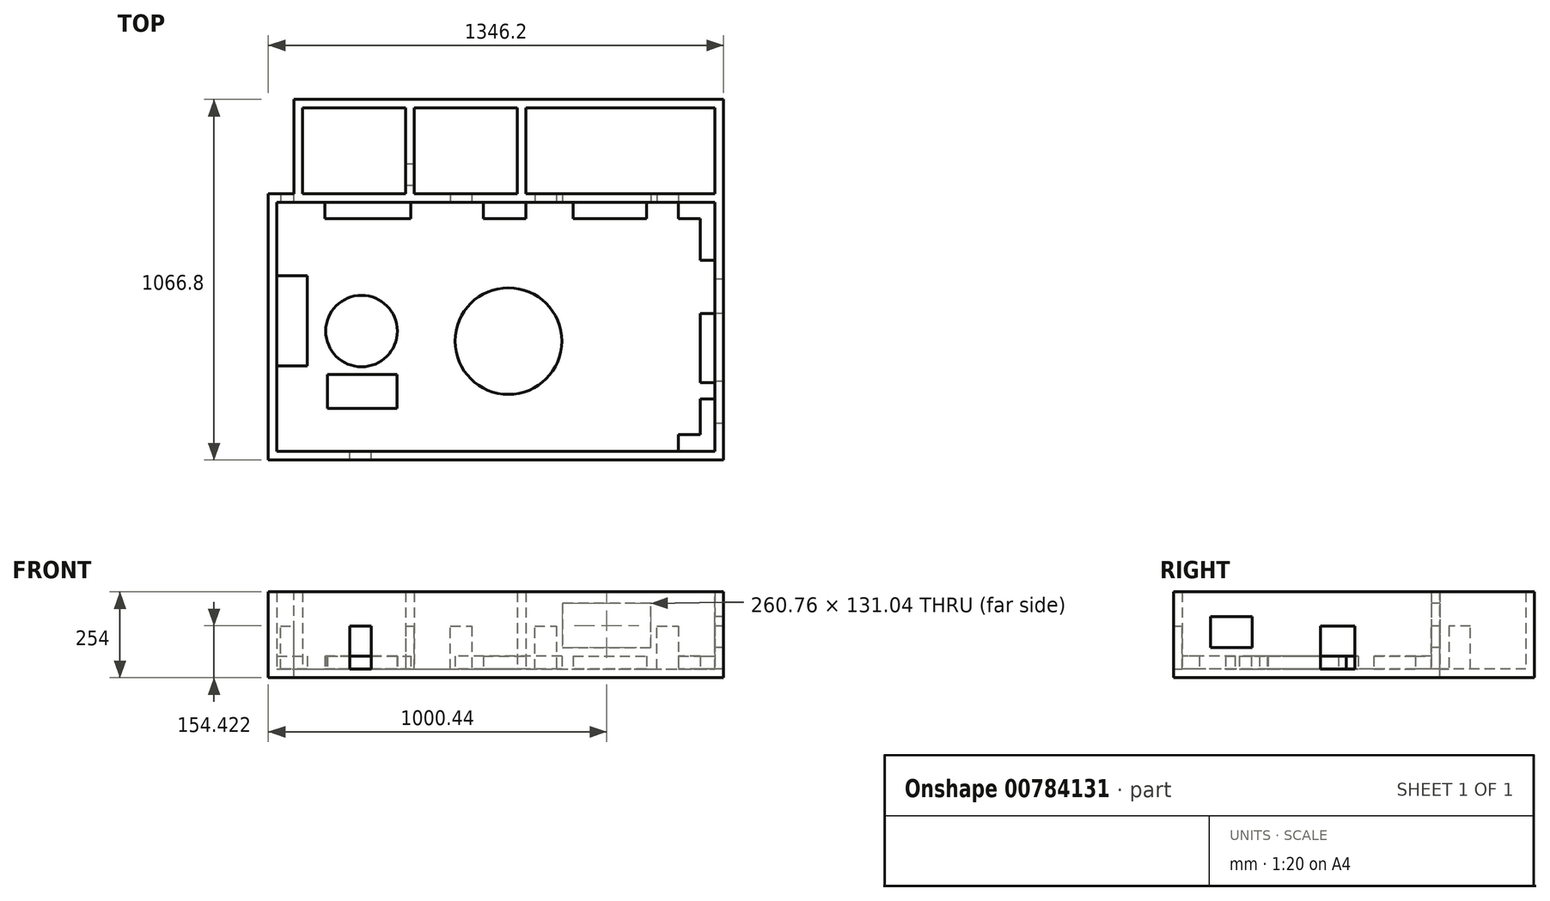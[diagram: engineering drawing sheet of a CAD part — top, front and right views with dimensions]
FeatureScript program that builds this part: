
annotation { "Feature Type Name" : "Feature", "Feature Type Description" : "" }
export const myFeature = defineFeature(function(context is Context, id is Id, definition is map)
    precondition{}
    {
        {
            var Q0;
            Q0=qCreatedBy(makeId("Top.planeOp"),FACE);
            var sketch = newSketch(context, id + "F0", { "sketchPlane" : qUnion([Q0])});
            skLineSegment(sketch, "E0.bottom", {"start": v(-673.24, 405.83) * mm, "end": v(672.96, 405.83) * mm});
            skLineSegment(sketch, "E0.top", {"start": v(-673.24, -381.57) * mm, "end": v(672.96, -381.57) * mm});
            skLineSegment(sketch, "E0.left", {"start": v(-673.24, 405.83) * mm, "end": v(-673.24, -381.57) * mm});
            skLineSegment(sketch, "E0.right", {"start": v(672.96, 405.83) * mm, "end": v(672.96, -381.57) * mm});
            skSolve(sketch);
        }
        {
            var Q0;
            Q0 = qSketchRegion(id + "F0", true);
            extrude(context, id + "F1", {"entities" : qUnion([Q0]), "depth" : 254 * mm, "offsetDistance" : 25.4 * mm});
        }
        {
            var Q0;
            Q0=makeQuery(id+"F1.opExtrude","CAP_FACE",FACE,{"disambiguationData":[OSD([sQuery(id+"F0.wireOp",EDGE,"E0.bottom"),sQuery(id+"F0.wireOp",EDGE,"E0.top"),sQuery(id+"F0.wireOp",EDGE,"E0.left"),sQuery(id+"F0.wireOp",EDGE,"E0.right")])],"isStart":false});
            shell(context, id + "F2", {"entities" : qUnion([Q0]), "thickness" : 25.4 * mm});
        }
        {
            var Q0;
            Q0=makeQuery(id+"F1.opExtrude","SWEPT_FACE",FACE,{"disambiguationData":[OSD([sQuery(id+"F0.wireOp",EDGE,"E0.bottom")])]});
            var sketch = newSketch(context, id + "F3", { "sketchPlane" : qUnion([Q0])});
            skLineSegment(sketch, "E1", {"start": v(597.04, 0) * mm, "end": v(597.04, 254) * mm});
            skLineSegment(sketch, "E2", {"start": v(597.04, 254) * mm, "end": v(-672.96, 254) * mm});
            skLineSegment(sketch, "E3", {"start": v(-672.96, 254) * mm, "end": v(-672.96, 0) * mm});
            skLineSegment(sketch, "E4", {"start": v(-672.96, 0) * mm, "end": v(597.04, 0) * mm});
            skSolve(sketch);
        }
        {
            var Q0;
            Q0 = qSketchRegion(id + "F3", true);
            extrude(context, id + "F4", {"entities" : qUnion([Q0]), "operationType" : NewBodyOperationType.ADD, "depth" : 279.4 * mm, "offsetDistance" : 25.4 * mm});
        }
        {
            var Q0;
            Q0=makeQuery(id+"F4.boolean.opBoolean","MERGE",FACE,{"derivedFrom":[makeQuery(id+"F1.opExtrude","CAP_FACE",FACE,{"disambiguationData":[OSD([sQuery(id+"F0.wireOp",EDGE,"E0.bottom"),sQuery(id+"F0.wireOp",EDGE,"E0.top"),sQuery(id+"F0.wireOp",EDGE,"E0.left"),sQuery(id+"F0.wireOp",EDGE,"E0.right")])],"isStart":false}),makeQuery(id+"F4.opExtrude","SWEPT_FACE",FACE,{"disambiguationData":[OSD([sQuery(id+"F3.wireOp",EDGE,"E2")])]})]});
            shell(context, id + "F5", {"entities" : qUnion([Q0]), "thickness" : 25.4 * mm});
        }
        {
            var Q0;
            Q0=makeQuery(id+"F5.opShell","OFFSET_FACE",FACE,{"disambiguationData":[OSD([sQuery(id+"F0.wireOp",EDGE,"E0.bottom"),sQuery(id+"F0.wireOp",EDGE,"E0.top"),sQuery(id+"F0.wireOp",EDGE,"E0.left"),sQuery(id+"F0.wireOp",EDGE,"E0.right"),sQuery(id+"F3.wireOp",EDGE,"E4")])]});
            var sketch = newSketch(context, id + "F6", { "sketchPlane" : qUnion([Q0])});
            skLineSegment(sketch, "E5", {"start": v(-266.84, 405.83) * mm, "end": v(-266.84, 659.83) * mm});
            skLineSegment(sketch, "E6", {"start": v(-266.84, 659.83) * mm, "end": v(-241.44, 659.83) * mm});
            skLineSegment(sketch, "E7", {"start": v(-241.44, 659.83) * mm, "end": v(-241.44, 405.83) * mm});
            skLineSegment(sketch, "E8", {"start": v(-241.44, 405.83) * mm, "end": v(-266.84, 405.83) * mm});
            skSolve(sketch);
        }
        {
            var Q0;
            Q0=makeQuery(id+"F6.imprint","IMPRINT",FACE,{"disambiguationData":[TD([[makeQuery(id+"F6.imprint","IMPRINT",EDGE,{"derivedFrom":sQuery(id+"F6.wireOp",EDGE,"E5")}),-1.0]])]});
            extrude(context, id + "F7", {"entities" : qUnion([Q0]), "operationType" : NewBodyOperationType.ADD, "depth" : 228.6 * mm, "offsetDistance" : 25.4 * mm});
        }
        {
            var Q0;
            Q0=makeQuery(id+"F7.opExtrude","SWEPT_FACE",FACE,{"disambiguationData":[OSD([sQuery(id+"F6.wireOp",EDGE,"E7")])]});
            var sketch = newSketch(context, id + "F8", { "sketchPlane" : qUnion([Q0])});
            skLineSegment(sketch, "E9", {"start": v(495.71, 25.4) * mm, "end": v(495.71, 152.4) * mm});
            skLineSegment(sketch, "E10", {"start": v(495.71, 152.4) * mm, "end": v(432.21, 152.4) * mm});
            skLineSegment(sketch, "E11", {"start": v(432.21, 152.4) * mm, "end": v(432.21, 25.4) * mm});
            skLineSegment(sketch, "E12", {"start": v(432.21, 25.4) * mm, "end": v(495.71, 25.4) * mm});
            skSolve(sketch);
        }
        {
            var Q0;
            Q0 = qSketchRegion(id + "F8", true);
            extrude(context, id + "F9", {"entities" : qUnion([Q0]), "operationType" : NewBodyOperationType.REMOVE, "oppositeDirection" : true, "depth" : 25.4 * mm, "offsetDistance" : 25.4 * mm});
        }
        {
            var Q0;
            {var subQ0=sQuery(id+"F0.wireOp",EDGE,"E0.bottom");var subQ2=sQuery(id+"F3.wireOp",EDGE,"E4");var subQ4=sQuery(id+"F3.wireOp",EDGE,"E1");var subQ6=sQuery(id+"F0.wireOp",EDGE,"E0.right");var subQ7=makeQuery(id+"F5.opShell","OFFSET_FACE",FACE,{"disambiguationData":[OSD([subQ0,sQuery(id+"F0.wireOp",EDGE,"E0.top"),sQuery(id+"F0.wireOp",EDGE,"E0.left"),subQ6,subQ2])]});Q0=makeQuery(id+"F9.boolean.opBoolean","MERGE",FACE,{"derivedFrom":[makeQuery(id+"F7.boolean.opBoolean","SPLIT",FACE,{"disambiguationData":[TD([makeQuery(id+"F5.opShell","OFFSET_FACE",FACE,{"disambiguationData":[OSD([subQ4])]})])],"derivedFrom":subQ7}),makeQuery(id+"F7.boolean.opBoolean","SPLIT",FACE,{"disambiguationData":[TD([makeQuery(id+"F7.opExtrude","SWEPT_FACE",FACE,{"disambiguationData":[OSD([sQuery(id+"F6.wireOp",EDGE,"E7")])]})])],"derivedFrom":subQ7}),makeQuery(id+"F9.opExtrude","SWEPT_FACE",FACE,{"disambiguationData":[OSD([sQuery(id+"F8.wireOp",EDGE,"E12")])]})]});}
            var sketch = newSketch(context, id + "F10", { "sketchPlane" : qUnion([Q0])});
            skLineSegment(sketch, "E13", {"start": v(63.36, 405.83) * mm, "end": v(63.36, 659.83) * mm});
            skLineSegment(sketch, "E14", {"start": v(63.36, 659.83) * mm, "end": v(88.76, 659.83) * mm});
            skLineSegment(sketch, "E15", {"start": v(88.76, 659.83) * mm, "end": v(88.76, 405.83) * mm});
            skLineSegment(sketch, "E16", {"start": v(88.76, 405.83) * mm, "end": v(63.36, 405.83) * mm});
            skSolve(sketch);
        }
        {
            var Q0;
            Q0=makeQuery(id+"F10.imprint","IMPRINT",FACE,{"disambiguationData":[TD([[makeQuery(id+"F10.imprint","IMPRINT",EDGE,{"derivedFrom":sQuery(id+"F10.wireOp",EDGE,"E13")}),-1.0]])]});
            extrude(context, id + "F11", {"entities" : qUnion([Q0]), "operationType" : NewBodyOperationType.ADD, "depth" : 228.6 * mm, "offsetDistance" : 25.4 * mm});
        }
        {
            var Q0;
            Q0=makeQuery(id+"F2.opShell","OFFSET_FACE",FACE,{"disambiguationData":[OSD([sQuery(id+"F0.wireOp",EDGE,"E0.bottom")])]});
            var sketch = newSketch(context, id + "F12", { "sketchPlane" : qUnion([Q0])});
            skLineSegment(sketch, "E17", {"start": v(-134.67, 25.4) * mm, "end": v(-134.67, 152.4) * mm});
            skLineSegment(sketch, "E18", {"start": v(-134.67, 152.4) * mm, "end": v(-71.17, 152.4) * mm});
            skLineSegment(sketch, "E19", {"start": v(-71.17, 152.4) * mm, "end": v(-71.17, 25.4) * mm});
            skLineSegment(sketch, "E20", {"start": v(-71.17, 25.4) * mm, "end": v(-134.67, 25.4) * mm});
            skSolve(sketch);
        }
        {
            var Q0;
            Q0=makeQuery(id+"F12.imprint","IMPRINT",FACE,{"disambiguationData":[TD([[makeQuery(id+"F12.imprint","IMPRINT",EDGE,{"derivedFrom":sQuery(id+"F12.wireOp",EDGE,"E17")}),-1.0]])]});
            extrude(context, id + "F13", {"entities" : qUnion([Q0]), "operationType" : NewBodyOperationType.REMOVE, "oppositeDirection" : true, "depth" : 25.4 * mm, "offsetDistance" : 25.4 * mm});
        }
        {
            var Q0;
            Q0=makeQuery(id+"F2.opShell","OFFSET_FACE",FACE,{"disambiguationData":[OSD([sQuery(id+"F0.wireOp",EDGE,"E0.bottom")])]});
            var sketch = newSketch(context, id + "F14", { "sketchPlane" : qUnion([Q0])});
            skLineSegment(sketch, "E21", {"start": v(114.87, 25.4) * mm, "end": v(114.87, 152.4) * mm});
            skLineSegment(sketch, "E22", {"start": v(114.87, 152.4) * mm, "end": v(178.37, 152.4) * mm});
            skLineSegment(sketch, "E23", {"start": v(178.37, 152.4) * mm, "end": v(178.37, 25.4) * mm});
            skLineSegment(sketch, "E24", {"start": v(178.37, 25.4) * mm, "end": v(114.87, 25.4) * mm});
            skLineSegment(sketch, "E25", {"start": v(476.16, 25.4) * mm, "end": v(476.16, 152.4) * mm});
            skLineSegment(sketch, "E26", {"start": v(476.16, 152.4) * mm, "end": v(539.66, 152.4) * mm});
            skLineSegment(sketch, "E27", {"start": v(539.66, 152.4) * mm, "end": v(539.66, 25.4) * mm});
            skLineSegment(sketch, "E28", {"start": v(539.66, 25.4) * mm, "end": v(476.16, 25.4) * mm});
            skSolve(sketch);
        }
        {
            var Q0;
            Q0 = qSketchRegion(id + "F14", true);
            extrude(context, id + "F15", {"entities" : qUnion([Q0]), "operationType" : NewBodyOperationType.REMOVE, "oppositeDirection" : true, "depth" : 25.4 * mm, "offsetDistance" : 25.4 * mm});
        }
        {
            var Q0;
            Q0=makeQuery(id+"F2.opShell","OFFSET_FACE",FACE,{"disambiguationData":[OSD([sQuery(id+"F0.wireOp",EDGE,"E0.top")])]});
            var sketch = newSketch(context, id + "F16", { "sketchPlane" : qUnion([Q0])});
            skLineSegment(sketch, "E29", {"start": v(368.37, 25.4) * mm, "end": v(368.37, 152.4) * mm});
            skLineSegment(sketch, "E30", {"start": v(368.37, 152.4) * mm, "end": v(431.87, 152.4) * mm});
            skLineSegment(sketch, "E31", {"start": v(431.87, 152.4) * mm, "end": v(431.87, 25.4) * mm});
            skLineSegment(sketch, "E32", {"start": v(431.87, 25.4) * mm, "end": v(368.37, 25.4) * mm});
            skSolve(sketch);
        }
        {
            var Q0;
            Q0 = qSketchRegion(id + "F16", true);
            extrude(context, id + "F17", {"entities" : qUnion([Q0]), "operationType" : NewBodyOperationType.REMOVE, "oppositeDirection" : true, "depth" : 25.4 * mm, "offsetDistance" : 25.4 * mm});
        }
        {
            var Q0;
            Q0=makeQuery(id+"F2.opShell","OFFSET_FACE",FACE,{"disambiguationData":[OSD([sQuery(id+"F0.wireOp",EDGE,"E0.right")])]});
            var sketch = newSketch(context, id + "F18", { "sketchPlane" : qUnion([Q0])});
            skLineSegment(sketch, "E33", {"start": v(-153.76, 25.4) * mm, "end": v(-153.76, 152.4) * mm});
            skLineSegment(sketch, "E34", {"start": v(-153.76, 152.4) * mm, "end": v(-52.16, 152.4) * mm});
            skLineSegment(sketch, "E35", {"start": v(-52.16, 152.4) * mm, "end": v(-52.16, 25.4) * mm});
            skLineSegment(sketch, "E36", {"start": v(-52.16, 25.4) * mm, "end": v(-153.76, 25.4) * mm});
            skSolve(sketch);
        }
        {
            var Q0;
            Q0 = qSketchRegion(id + "F18", true);
            extrude(context, id + "F19", {"entities" : qUnion([Q0]), "operationType" : NewBodyOperationType.REMOVE, "oppositeDirection" : true, "depth" : 25.4 * mm, "offsetDistance" : 25.4 * mm});
        }
        {
            var Q0;
            Q0=makeQuery(id+"F2.opShell","OFFSET_FACE",FACE,{"disambiguationData":[OSD([sQuery(id+"F0.wireOp",EDGE,"E0.bottom")])]});
            var sketch = newSketch(context, id + "F20", { "sketchPlane" : qUnion([Q0])});
            skLineSegment(sketch, "E37", {"start": v(196.82, 88.9) * mm, "end": v(457.58, 88.9) * mm});
            skPoint(sketch, "E37.startSnap0", {"position": v(178.37, 88.9) * mm});
            skLineSegment(sketch, "E38", {"start": v(457.58, 88.9) * mm, "end": v(457.58, 219.94) * mm});
            skLineSegment(sketch, "E39", {"start": v(457.58, 219.94) * mm, "end": v(196.82, 219.94) * mm});
            skLineSegment(sketch, "E40", {"start": v(196.82, 219.94) * mm, "end": v(196.82, 88.9) * mm});
            skSolve(sketch);
        }
        {
            var Q0;
            Q0 = qSketchRegion(id + "F20", true);
            extrude(context, id + "F21", {"entities" : qUnion([Q0]), "operationType" : NewBodyOperationType.REMOVE, "oppositeDirection" : true, "depth" : 25.4 * mm, "offsetDistance" : 25.4 * mm});
        }
        {
            var Q0;
            Q0=makeQuery(id+"F2.opShell","OFFSET_FACE",FACE,{"disambiguationData":[OSD([sQuery(id+"F0.wireOp",EDGE,"E0.right")])]});
            var sketch = newSketch(context, id + "F22", { "sketchPlane" : qUnion([Q0])});
            skLineSegment(sketch, "E41", {"start": v(149.12, 88.9) * mm, "end": v(149.12, 180.64) * mm});
            skPoint(sketch, "E41.startSnap0", {"position": v(-52.16, 88.9) * mm});
            skLineSegment(sketch, "E42", {"start": v(149.12, 180.64) * mm, "end": v(273.32, 180.64) * mm});
            skLineSegment(sketch, "E43", {"start": v(273.32, 180.64) * mm, "end": v(273.32, 88.9) * mm});
            skLineSegment(sketch, "E44", {"start": v(273.32, 88.9) * mm, "end": v(149.12, 88.9) * mm});
            skSolve(sketch);
        }
        {
            var Q0;
            Q0 = qSketchRegion(id + "F22", true);
            extrude(context, id + "F23", {"entities" : qUnion([Q0]), "operationType" : NewBodyOperationType.REMOVE, "oppositeDirection" : true, "depth" : 25.4 * mm, "offsetDistance" : 25.4 * mm});
        }
        {
            var Q0;
            Q0=makeQuery(id+"F2.opShell","OFFSET_FACE",FACE,{"disambiguationData":[OSD([sQuery(id+"F0.wireOp",EDGE,"E0.bottom")])]});
            var sketch = newSketch(context, id + "F24", { "sketchPlane" : qUnion([Q0])});
            skLineSegment(sketch, "E45", {"start": v(-637.18, 25.4) * mm, "end": v(-637.18, 152.4) * mm});
            skLineSegment(sketch, "E46", {"start": v(-637.18, 152.4) * mm, "end": v(-599.08, 152.4) * mm});
            skLineSegment(sketch, "E47", {"start": v(-599.08, 152.4) * mm, "end": v(-599.08, 25.4) * mm});
            skLineSegment(sketch, "E48", {"start": v(-599.08, 25.4) * mm, "end": v(-637.18, 25.4) * mm});
            skSolve(sketch);
        }
        {
            var Q0;
            Q0 = qSketchRegion(id + "F24", true);
            extrude(context, id + "F25", {"entities" : qUnion([Q0]), "operationType" : NewBodyOperationType.REMOVE, "oppositeDirection" : true, "depth" : 25.4 * mm, "offsetDistance" : 25.4 * mm});
        }
        {
            var Q0;
            {var subQ1=sQuery(id+"F3.wireOp",EDGE,"E1");var subQ2=makeQuery(id+"F5.opShell","OFFSET_FACE",FACE,{"disambiguationData":[OSD([subQ1])]});var subQ3=sQuery(id+"F3.wireOp",EDGE,"E4");var subQ6=sQuery(id+"F0.wireOp",EDGE,"E0.bottom");var subQ8=makeQuery(id+"F7.opExtrude","SWEPT_FACE",FACE,{"disambiguationData":[OSD([sQuery(id+"F6.wireOp",EDGE,"E7")])]});var subQ9=sQuery(id+"F0.wireOp",EDGE,"E0.right");var subQ11=sQuery(id+"F0.wireOp",EDGE,"E0.left");var subQ12=sQuery(id+"F0.wireOp",EDGE,"E0.top");var subQ13=makeQuery(id+"F5.opShell","OFFSET_FACE",FACE,{"disambiguationData":[OSD([subQ6,subQ12,subQ11,subQ9,subQ3])]});var subQ14=makeQuery(id+"F9.boolean.opBoolean","MERGE",FACE,{"derivedFrom":[makeQuery(id+"F7.boolean.opBoolean","SPLIT",FACE,{"disambiguationData":[TD([subQ2])],"derivedFrom":subQ13}),makeQuery(id+"F7.boolean.opBoolean","SPLIT",FACE,{"disambiguationData":[TD([subQ8])],"derivedFrom":subQ13}),makeQuery(id+"F9.opExtrude","SWEPT_FACE",FACE,{"disambiguationData":[OSD([sQuery(id+"F8.wireOp",EDGE,"E12")])]})]});Q0=makeQuery(id+"F25.boolean.opBoolean","MERGE",FACE,{"derivedFrom":[makeQuery(id+"F19.boolean.opBoolean","MERGE",FACE,{"derivedFrom":[makeQuery(id+"F17.boolean.opBoolean","MERGE",FACE,{"derivedFrom":[makeQuery(id+"F15.boolean.opBoolean","MERGE",FACE,{"derivedFrom":[makeQuery(id+"F11.boolean.opBoolean","SPLIT",FACE,{"disambiguationData":[TD([makeQuery(id+"F11.opExtrude","SWEPT_FACE",FACE,{"disambiguationData":[OSD([sQuery(id+"F10.wireOp",EDGE,"E15")])]})])],"derivedFrom":subQ14}),makeQuery(id+"F13.boolean.opBoolean","MERGE",FACE,{"derivedFrom":[makeQuery(id+"F2.opShell","OFFSET_FACE",FACE,{"disambiguationData":[OSD([subQ6,subQ12,subQ11,subQ9])]}),makeQuery(id+"F11.boolean.opBoolean","SPLIT",FACE,{"disambiguationData":[TD([subQ2])],"derivedFrom":subQ14}),makeQuery(id+"F13.opExtrude","SWEPT_FACE",FACE,{"disambiguationData":[OSD([sQuery(id+"F12.wireOp",EDGE,"E20")])]})]}),makeQuery(id+"F15.opExtrude","SWEPT_FACE",FACE,{"disambiguationData":[OSD([sQuery(id+"F14.wireOp",EDGE,"E24")])]}),makeQuery(id+"F15.opExtrude","SWEPT_FACE",FACE,{"disambiguationData":[OSD([sQuery(id+"F14.wireOp",EDGE,"E28")])]})]}),makeQuery(id+"F17.opExtrude","SWEPT_FACE",FACE,{"disambiguationData":[OSD([sQuery(id+"F16.wireOp",EDGE,"E32")])]})]}),makeQuery(id+"F19.opExtrude","SWEPT_FACE",FACE,{"disambiguationData":[OSD([sQuery(id+"F18.wireOp",EDGE,"E36")])]})]}),makeQuery(id+"F25.opExtrude","SWEPT_FACE",FACE,{"disambiguationData":[OSD([sQuery(id+"F24.wireOp",EDGE,"E48")])]})]});}
            var sketch = newSketch(context, id + "F26", { "sketchPlane" : qUnion([Q0])});
            skLineSegment(sketch, "E49", {"start": v(539.66, 380.43) * mm, "end": v(647.56, 380.43) * mm});
            skLineSegment(sketch, "E50", {"start": v(647.56, 380.43) * mm, "end": v(647.56, 209.54) * mm});
            skLineSegment(sketch, "E51", {"start": v(647.56, 209.54) * mm, "end": v(604.15, 209.54) * mm});
            skLineSegment(sketch, "E52", {"start": v(604.15, 209.54) * mm, "end": v(604.15, 332.77) * mm});
            skLineSegment(sketch, "E53", {"start": v(604.15, 332.77) * mm, "end": v(539.66, 332.77) * mm});
            skLineSegment(sketch, "E54", {"start": v(539.66, 332.77) * mm, "end": v(539.66, 380.43) * mm});
            skLineSegment(sketch, "E55", {"start": v(647.56, 52.16) * mm, "end": v(647.56, -152) * mm});
            skLineSegment(sketch, "E56", {"start": v(647.56, -152) * mm, "end": v(604.15, -152) * mm});
            skLineSegment(sketch, "E57", {"start": v(604.15, -152) * mm, "end": v(604.15, 52.16) * mm});
            skLineSegment(sketch, "E58", {"start": v(604.15, 52.16) * mm, "end": v(647.56, 52.16) * mm});
            skLineSegment(sketch, "E59", {"start": v(647.56, -200.4) * mm, "end": v(604.15, -200.4) * mm});
            skLineSegment(sketch, "E60", {"start": v(604.15, -200.4) * mm, "end": v(604.15, -305.96) * mm});
            skLineSegment(sketch, "E61", {"start": v(604.15, -305.96) * mm, "end": v(539.66, -305.96) * mm});
            skLineSegment(sketch, "E62", {"start": v(539.66, -305.96) * mm, "end": v(539.66, -356.17) * mm});
            skLineSegment(sketch, "E63", {"start": v(539.66, -356.17) * mm, "end": v(647.56, -356.17) * mm});
            skLineSegment(sketch, "E64", {"start": v(647.56, -356.17) * mm, "end": v(647.56, -200.4) * mm});
            skSolve(sketch);
        }
        {
            var Q0;
            Q0=makeQuery(id+"F26.imprint","IMPRINT",FACE,{"disambiguationData":[TD([[makeQuery(id+"F26.imprint","IMPRINT",EDGE,{"derivedFrom":sQuery(id+"F26.wireOp",EDGE,"E49")}),-1.0]])]});
            var Q1;
            Q1=makeQuery(id+"F26.imprint","IMPRINT",FACE,{"disambiguationData":[TD([[makeQuery(id+"F26.imprint","IMPRINT",EDGE,{"derivedFrom":sQuery(id+"F26.wireOp",EDGE,"E55")}),-1.0]])]});
            var Q2;
            Q2=makeQuery(id+"F26.imprint","IMPRINT",FACE,{"disambiguationData":[TD([[makeQuery(id+"F26.imprint","IMPRINT",EDGE,{"derivedFrom":sQuery(id+"F26.wireOp",EDGE,"E59")}),1.0]])]});
            extrude(context, id + "F27", {"entities" : qUnion([Q0, Q1, Q2]), "operationType" : NewBodyOperationType.ADD, "depth" : 38.1 * mm, "offsetDistance" : 25.4 * mm});
        }
        {
            var Q0;
            {var subQ1=sQuery(id+"F3.wireOp",EDGE,"E1");var subQ2=makeQuery(id+"F5.opShell","OFFSET_FACE",FACE,{"disambiguationData":[OSD([subQ1])]});var subQ3=sQuery(id+"F3.wireOp",EDGE,"E4");var subQ6=sQuery(id+"F0.wireOp",EDGE,"E0.bottom");var subQ8=makeQuery(id+"F7.opExtrude","SWEPT_FACE",FACE,{"disambiguationData":[OSD([sQuery(id+"F6.wireOp",EDGE,"E7")])]});var subQ9=sQuery(id+"F0.wireOp",EDGE,"E0.right");var subQ11=sQuery(id+"F0.wireOp",EDGE,"E0.left");var subQ12=sQuery(id+"F0.wireOp",EDGE,"E0.top");var subQ13=makeQuery(id+"F5.opShell","OFFSET_FACE",FACE,{"disambiguationData":[OSD([subQ6,subQ12,subQ11,subQ9,subQ3])]});var subQ14=makeQuery(id+"F9.boolean.opBoolean","MERGE",FACE,{"derivedFrom":[makeQuery(id+"F7.boolean.opBoolean","SPLIT",FACE,{"disambiguationData":[TD([subQ2])],"derivedFrom":subQ13}),makeQuery(id+"F7.boolean.opBoolean","SPLIT",FACE,{"disambiguationData":[TD([subQ8])],"derivedFrom":subQ13}),makeQuery(id+"F9.opExtrude","SWEPT_FACE",FACE,{"disambiguationData":[OSD([sQuery(id+"F8.wireOp",EDGE,"E12")])]})]});Q0=makeQuery(id+"F25.boolean.opBoolean","MERGE",FACE,{"derivedFrom":[makeQuery(id+"F19.boolean.opBoolean","MERGE",FACE,{"derivedFrom":[makeQuery(id+"F17.boolean.opBoolean","MERGE",FACE,{"derivedFrom":[makeQuery(id+"F15.boolean.opBoolean","MERGE",FACE,{"derivedFrom":[makeQuery(id+"F11.boolean.opBoolean","SPLIT",FACE,{"disambiguationData":[TD([makeQuery(id+"F11.opExtrude","SWEPT_FACE",FACE,{"disambiguationData":[OSD([sQuery(id+"F10.wireOp",EDGE,"E15")])]})])],"derivedFrom":subQ14}),makeQuery(id+"F13.boolean.opBoolean","MERGE",FACE,{"derivedFrom":[makeQuery(id+"F2.opShell","OFFSET_FACE",FACE,{"disambiguationData":[OSD([subQ6,subQ12,subQ11,subQ9])]}),makeQuery(id+"F11.boolean.opBoolean","SPLIT",FACE,{"disambiguationData":[TD([subQ2])],"derivedFrom":subQ14}),makeQuery(id+"F13.opExtrude","SWEPT_FACE",FACE,{"disambiguationData":[OSD([sQuery(id+"F12.wireOp",EDGE,"E20")])]})]}),makeQuery(id+"F15.opExtrude","SWEPT_FACE",FACE,{"disambiguationData":[OSD([sQuery(id+"F14.wireOp",EDGE,"E24")])]}),makeQuery(id+"F15.opExtrude","SWEPT_FACE",FACE,{"disambiguationData":[OSD([sQuery(id+"F14.wireOp",EDGE,"E28")])]})]}),makeQuery(id+"F17.opExtrude","SWEPT_FACE",FACE,{"disambiguationData":[OSD([sQuery(id+"F16.wireOp",EDGE,"E32")])]})]}),makeQuery(id+"F19.opExtrude","SWEPT_FACE",FACE,{"disambiguationData":[OSD([sQuery(id+"F18.wireOp",EDGE,"E36")])]})]}),makeQuery(id+"F25.opExtrude","SWEPT_FACE",FACE,{"disambiguationData":[OSD([sQuery(id+"F24.wireOp",EDGE,"E48")])]})]});}
            var sketch = newSketch(context, id + "F28", { "sketchPlane" : qUnion([Q0])});
            skLineSegment(sketch, "E65", {"start": v(228.12, 380.43) * mm, "end": v(445.26, 380.43) * mm});
            skLineSegment(sketch, "E66", {"start": v(445.26, 380.43) * mm, "end": v(445.26, 332.77) * mm});
            skLineSegment(sketch, "E67", {"start": v(445.26, 332.77) * mm, "end": v(228.12, 332.77) * mm});
            skLineSegment(sketch, "E68", {"start": v(228.12, 332.77) * mm, "end": v(228.12, 380.43) * mm});
            skSolve(sketch);
        }
        {
            var Q0;
            Q0 = qSketchRegion(id + "F28", true);
            extrude(context, id + "F29", {"entities" : qUnion([Q0]), "operationType" : NewBodyOperationType.ADD, "depth" : 38.1 * mm, "offsetDistance" : 25.4 * mm});
        }
        {
            var Q0;
            {var subQ1=sQuery(id+"F3.wireOp",EDGE,"E1");var subQ2=makeQuery(id+"F5.opShell","OFFSET_FACE",FACE,{"disambiguationData":[OSD([subQ1])]});var subQ3=sQuery(id+"F3.wireOp",EDGE,"E4");var subQ6=sQuery(id+"F0.wireOp",EDGE,"E0.bottom");var subQ8=makeQuery(id+"F7.opExtrude","SWEPT_FACE",FACE,{"disambiguationData":[OSD([sQuery(id+"F6.wireOp",EDGE,"E7")])]});var subQ9=sQuery(id+"F0.wireOp",EDGE,"E0.right");var subQ11=sQuery(id+"F0.wireOp",EDGE,"E0.left");var subQ12=sQuery(id+"F0.wireOp",EDGE,"E0.top");var subQ13=makeQuery(id+"F5.opShell","OFFSET_FACE",FACE,{"disambiguationData":[OSD([subQ6,subQ12,subQ11,subQ9,subQ3])]});var subQ14=makeQuery(id+"F9.boolean.opBoolean","MERGE",FACE,{"derivedFrom":[makeQuery(id+"F7.boolean.opBoolean","SPLIT",FACE,{"disambiguationData":[TD([subQ2])],"derivedFrom":subQ13}),makeQuery(id+"F7.boolean.opBoolean","SPLIT",FACE,{"disambiguationData":[TD([subQ8])],"derivedFrom":subQ13}),makeQuery(id+"F9.opExtrude","SWEPT_FACE",FACE,{"disambiguationData":[OSD([sQuery(id+"F8.wireOp",EDGE,"E12")])]})]});Q0=makeQuery(id+"F25.boolean.opBoolean","MERGE",FACE,{"derivedFrom":[makeQuery(id+"F19.boolean.opBoolean","MERGE",FACE,{"derivedFrom":[makeQuery(id+"F17.boolean.opBoolean","MERGE",FACE,{"derivedFrom":[makeQuery(id+"F15.boolean.opBoolean","MERGE",FACE,{"derivedFrom":[makeQuery(id+"F11.boolean.opBoolean","SPLIT",FACE,{"disambiguationData":[TD([makeQuery(id+"F11.opExtrude","SWEPT_FACE",FACE,{"disambiguationData":[OSD([sQuery(id+"F10.wireOp",EDGE,"E15")])]})])],"derivedFrom":subQ14}),makeQuery(id+"F13.boolean.opBoolean","MERGE",FACE,{"derivedFrom":[makeQuery(id+"F2.opShell","OFFSET_FACE",FACE,{"disambiguationData":[OSD([subQ6,subQ12,subQ11,subQ9])]}),makeQuery(id+"F11.boolean.opBoolean","SPLIT",FACE,{"disambiguationData":[TD([subQ2])],"derivedFrom":subQ14}),makeQuery(id+"F13.opExtrude","SWEPT_FACE",FACE,{"disambiguationData":[OSD([sQuery(id+"F12.wireOp",EDGE,"E20")])]})]}),makeQuery(id+"F15.opExtrude","SWEPT_FACE",FACE,{"disambiguationData":[OSD([sQuery(id+"F14.wireOp",EDGE,"E24")])]}),makeQuery(id+"F15.opExtrude","SWEPT_FACE",FACE,{"disambiguationData":[OSD([sQuery(id+"F14.wireOp",EDGE,"E28")])]})]}),makeQuery(id+"F17.opExtrude","SWEPT_FACE",FACE,{"disambiguationData":[OSD([sQuery(id+"F16.wireOp",EDGE,"E32")])]})]}),makeQuery(id+"F19.opExtrude","SWEPT_FACE",FACE,{"disambiguationData":[OSD([sQuery(id+"F18.wireOp",EDGE,"E36")])]})]}),makeQuery(id+"F25.opExtrude","SWEPT_FACE",FACE,{"disambiguationData":[OSD([sQuery(id+"F24.wireOp",EDGE,"E48")])]})]});}
            var sketch = newSketch(context, id + "F30", { "sketchPlane" : qUnion([Q0])});
            skLineSegment(sketch, "E69", {"start": v(-37.6, 380.43) * mm, "end": v(88.76, 380.43) * mm});
            skLineSegment(sketch, "E70", {"start": v(88.76, 380.43) * mm, "end": v(88.76, 332.77) * mm});
            skLineSegment(sketch, "E71", {"start": v(88.76, 332.77) * mm, "end": v(-37.6, 332.77) * mm});
            skLineSegment(sketch, "E72", {"start": v(-37.6, 332.77) * mm, "end": v(-37.6, 380.43) * mm});
            skSolve(sketch);
        }
        {
            var Q0;
            Q0 = qSketchRegion(id + "F30", true);
            extrude(context, id + "F31", {"entities" : qUnion([Q0]), "operationType" : NewBodyOperationType.ADD, "depth" : 38.1 * mm, "offsetDistance" : 25.4 * mm});
        }
        {
            var Q0;
            {var subQ1=sQuery(id+"F3.wireOp",EDGE,"E1");var subQ2=makeQuery(id+"F5.opShell","OFFSET_FACE",FACE,{"disambiguationData":[OSD([subQ1])]});var subQ3=sQuery(id+"F3.wireOp",EDGE,"E4");var subQ6=sQuery(id+"F0.wireOp",EDGE,"E0.bottom");var subQ8=makeQuery(id+"F7.opExtrude","SWEPT_FACE",FACE,{"disambiguationData":[OSD([sQuery(id+"F6.wireOp",EDGE,"E7")])]});var subQ9=sQuery(id+"F0.wireOp",EDGE,"E0.right");var subQ11=sQuery(id+"F0.wireOp",EDGE,"E0.left");var subQ12=sQuery(id+"F0.wireOp",EDGE,"E0.top");var subQ13=makeQuery(id+"F5.opShell","OFFSET_FACE",FACE,{"disambiguationData":[OSD([subQ6,subQ12,subQ11,subQ9,subQ3])]});var subQ14=makeQuery(id+"F9.boolean.opBoolean","MERGE",FACE,{"derivedFrom":[makeQuery(id+"F7.boolean.opBoolean","SPLIT",FACE,{"disambiguationData":[TD([subQ2])],"derivedFrom":subQ13}),makeQuery(id+"F7.boolean.opBoolean","SPLIT",FACE,{"disambiguationData":[TD([subQ8])],"derivedFrom":subQ13}),makeQuery(id+"F9.opExtrude","SWEPT_FACE",FACE,{"disambiguationData":[OSD([sQuery(id+"F8.wireOp",EDGE,"E12")])]})]});Q0=makeQuery(id+"F25.boolean.opBoolean","MERGE",FACE,{"derivedFrom":[makeQuery(id+"F19.boolean.opBoolean","MERGE",FACE,{"derivedFrom":[makeQuery(id+"F17.boolean.opBoolean","MERGE",FACE,{"derivedFrom":[makeQuery(id+"F15.boolean.opBoolean","MERGE",FACE,{"derivedFrom":[makeQuery(id+"F11.boolean.opBoolean","SPLIT",FACE,{"disambiguationData":[TD([makeQuery(id+"F11.opExtrude","SWEPT_FACE",FACE,{"disambiguationData":[OSD([sQuery(id+"F10.wireOp",EDGE,"E15")])]})])],"derivedFrom":subQ14}),makeQuery(id+"F13.boolean.opBoolean","MERGE",FACE,{"derivedFrom":[makeQuery(id+"F2.opShell","OFFSET_FACE",FACE,{"disambiguationData":[OSD([subQ6,subQ12,subQ11,subQ9])]}),makeQuery(id+"F11.boolean.opBoolean","SPLIT",FACE,{"disambiguationData":[TD([subQ2])],"derivedFrom":subQ14}),makeQuery(id+"F13.opExtrude","SWEPT_FACE",FACE,{"disambiguationData":[OSD([sQuery(id+"F12.wireOp",EDGE,"E20")])]})]}),makeQuery(id+"F15.opExtrude","SWEPT_FACE",FACE,{"disambiguationData":[OSD([sQuery(id+"F14.wireOp",EDGE,"E24")])]}),makeQuery(id+"F15.opExtrude","SWEPT_FACE",FACE,{"disambiguationData":[OSD([sQuery(id+"F14.wireOp",EDGE,"E28")])]})]}),makeQuery(id+"F17.opExtrude","SWEPT_FACE",FACE,{"disambiguationData":[OSD([sQuery(id+"F16.wireOp",EDGE,"E32")])]})]}),makeQuery(id+"F19.opExtrude","SWEPT_FACE",FACE,{"disambiguationData":[OSD([sQuery(id+"F18.wireOp",EDGE,"E36")])]})]}),makeQuery(id+"F25.opExtrude","SWEPT_FACE",FACE,{"disambiguationData":[OSD([sQuery(id+"F24.wireOp",EDGE,"E48")])]})]});}
            var sketch = newSketch(context, id + "F32", { "sketchPlane" : qUnion([Q0])});
            skLineSegment(sketch, "E73", {"start": v(-505.9, 380.43) * mm, "end": v(-252.35, 380.43) * mm});
            skLineSegment(sketch, "E74", {"start": v(-252.35, 380.43) * mm, "end": v(-252.35, 332.77) * mm});
            skLineSegment(sketch, "E75", {"start": v(-252.35, 332.77) * mm, "end": v(-505.9, 332.77) * mm});
            skLineSegment(sketch, "E76", {"start": v(-505.9, 332.77) * mm, "end": v(-505.9, 380.43) * mm});
            skSolve(sketch);
        }
        {
            var Q0;
            Q0 = qSketchRegion(id + "F32", true);
            extrude(context, id + "F33", {"entities" : qUnion([Q0]), "operationType" : NewBodyOperationType.ADD, "depth" : 38.1 * mm, "offsetDistance" : 25.4 * mm});
        }
        {
            var Q0;
            {var subQ1=sQuery(id+"F3.wireOp",EDGE,"E1");var subQ2=makeQuery(id+"F5.opShell","OFFSET_FACE",FACE,{"disambiguationData":[OSD([subQ1])]});var subQ3=sQuery(id+"F3.wireOp",EDGE,"E4");var subQ6=sQuery(id+"F0.wireOp",EDGE,"E0.bottom");var subQ8=makeQuery(id+"F7.opExtrude","SWEPT_FACE",FACE,{"disambiguationData":[OSD([sQuery(id+"F6.wireOp",EDGE,"E7")])]});var subQ9=sQuery(id+"F0.wireOp",EDGE,"E0.right");var subQ11=sQuery(id+"F0.wireOp",EDGE,"E0.left");var subQ12=sQuery(id+"F0.wireOp",EDGE,"E0.top");var subQ13=makeQuery(id+"F5.opShell","OFFSET_FACE",FACE,{"disambiguationData":[OSD([subQ6,subQ12,subQ11,subQ9,subQ3])]});var subQ14=makeQuery(id+"F9.boolean.opBoolean","MERGE",FACE,{"derivedFrom":[makeQuery(id+"F7.boolean.opBoolean","SPLIT",FACE,{"disambiguationData":[TD([subQ2])],"derivedFrom":subQ13}),makeQuery(id+"F7.boolean.opBoolean","SPLIT",FACE,{"disambiguationData":[TD([subQ8])],"derivedFrom":subQ13}),makeQuery(id+"F9.opExtrude","SWEPT_FACE",FACE,{"disambiguationData":[OSD([sQuery(id+"F8.wireOp",EDGE,"E12")])]})]});Q0=makeQuery(id+"F25.boolean.opBoolean","MERGE",FACE,{"derivedFrom":[makeQuery(id+"F19.boolean.opBoolean","MERGE",FACE,{"derivedFrom":[makeQuery(id+"F17.boolean.opBoolean","MERGE",FACE,{"derivedFrom":[makeQuery(id+"F15.boolean.opBoolean","MERGE",FACE,{"derivedFrom":[makeQuery(id+"F11.boolean.opBoolean","SPLIT",FACE,{"disambiguationData":[TD([makeQuery(id+"F11.opExtrude","SWEPT_FACE",FACE,{"disambiguationData":[OSD([sQuery(id+"F10.wireOp",EDGE,"E15")])]})])],"derivedFrom":subQ14}),makeQuery(id+"F13.boolean.opBoolean","MERGE",FACE,{"derivedFrom":[makeQuery(id+"F2.opShell","OFFSET_FACE",FACE,{"disambiguationData":[OSD([subQ6,subQ12,subQ11,subQ9])]}),makeQuery(id+"F11.boolean.opBoolean","SPLIT",FACE,{"disambiguationData":[TD([subQ2])],"derivedFrom":subQ14}),makeQuery(id+"F13.opExtrude","SWEPT_FACE",FACE,{"disambiguationData":[OSD([sQuery(id+"F12.wireOp",EDGE,"E20")])]})]}),makeQuery(id+"F15.opExtrude","SWEPT_FACE",FACE,{"disambiguationData":[OSD([sQuery(id+"F14.wireOp",EDGE,"E24")])]}),makeQuery(id+"F15.opExtrude","SWEPT_FACE",FACE,{"disambiguationData":[OSD([sQuery(id+"F14.wireOp",EDGE,"E28")])]})]}),makeQuery(id+"F17.opExtrude","SWEPT_FACE",FACE,{"disambiguationData":[OSD([sQuery(id+"F16.wireOp",EDGE,"E32")])]})]}),makeQuery(id+"F19.opExtrude","SWEPT_FACE",FACE,{"disambiguationData":[OSD([sQuery(id+"F18.wireOp",EDGE,"E36")])]})]}),makeQuery(id+"F25.opExtrude","SWEPT_FACE",FACE,{"disambiguationData":[OSD([sQuery(id+"F24.wireOp",EDGE,"E48")])]})]});}
            var sketch = newSketch(context, id + "F34", { "sketchPlane" : qUnion([Q0])});
            skLineSegment(sketch, "E77", {"start": v(-292.17, -228.52) * mm, "end": v(-292.17, -127.94) * mm});
            skLineSegment(sketch, "E78", {"start": v(-292.17, -127.94) * mm, "end": v(-498.18, -127.94) * mm});
            skLineSegment(sketch, "E79", {"start": v(-498.18, -127.94) * mm, "end": v(-498.18, -228.52) * mm});
            skLineSegment(sketch, "E80", {"start": v(-498.18, -228.52) * mm, "end": v(-292.17, -228.52) * mm});
            skSolve(sketch);
        }
        {
            var Q0;
            Q0 = qSketchRegion(id + "F34", true);
            extrude(context, id + "F35", {"entities" : qUnion([Q0]), "operationType" : NewBodyOperationType.ADD, "depth" : 38.1 * mm, "offsetDistance" : 25.4 * mm});
        }
        {
            var Q0;
            {var subQ1=sQuery(id+"F3.wireOp",EDGE,"E1");var subQ2=makeQuery(id+"F5.opShell","OFFSET_FACE",FACE,{"disambiguationData":[OSD([subQ1])]});var subQ3=sQuery(id+"F3.wireOp",EDGE,"E4");var subQ6=sQuery(id+"F0.wireOp",EDGE,"E0.bottom");var subQ8=makeQuery(id+"F7.opExtrude","SWEPT_FACE",FACE,{"disambiguationData":[OSD([sQuery(id+"F6.wireOp",EDGE,"E7")])]});var subQ9=sQuery(id+"F0.wireOp",EDGE,"E0.right");var subQ11=sQuery(id+"F0.wireOp",EDGE,"E0.left");var subQ12=sQuery(id+"F0.wireOp",EDGE,"E0.top");var subQ13=makeQuery(id+"F5.opShell","OFFSET_FACE",FACE,{"disambiguationData":[OSD([subQ6,subQ12,subQ11,subQ9,subQ3])]});var subQ14=makeQuery(id+"F9.boolean.opBoolean","MERGE",FACE,{"derivedFrom":[makeQuery(id+"F7.boolean.opBoolean","SPLIT",FACE,{"disambiguationData":[TD([subQ2])],"derivedFrom":subQ13}),makeQuery(id+"F7.boolean.opBoolean","SPLIT",FACE,{"disambiguationData":[TD([subQ8])],"derivedFrom":subQ13}),makeQuery(id+"F9.opExtrude","SWEPT_FACE",FACE,{"disambiguationData":[OSD([sQuery(id+"F8.wireOp",EDGE,"E12")])]})]});Q0=makeQuery(id+"F25.boolean.opBoolean","MERGE",FACE,{"derivedFrom":[makeQuery(id+"F19.boolean.opBoolean","MERGE",FACE,{"derivedFrom":[makeQuery(id+"F17.boolean.opBoolean","MERGE",FACE,{"derivedFrom":[makeQuery(id+"F15.boolean.opBoolean","MERGE",FACE,{"derivedFrom":[makeQuery(id+"F11.boolean.opBoolean","SPLIT",FACE,{"disambiguationData":[TD([makeQuery(id+"F11.opExtrude","SWEPT_FACE",FACE,{"disambiguationData":[OSD([sQuery(id+"F10.wireOp",EDGE,"E15")])]})])],"derivedFrom":subQ14}),makeQuery(id+"F13.boolean.opBoolean","MERGE",FACE,{"derivedFrom":[makeQuery(id+"F2.opShell","OFFSET_FACE",FACE,{"disambiguationData":[OSD([subQ6,subQ12,subQ11,subQ9])]}),makeQuery(id+"F11.boolean.opBoolean","SPLIT",FACE,{"disambiguationData":[TD([subQ2])],"derivedFrom":subQ14}),makeQuery(id+"F13.opExtrude","SWEPT_FACE",FACE,{"disambiguationData":[OSD([sQuery(id+"F12.wireOp",EDGE,"E20")])]})]}),makeQuery(id+"F15.opExtrude","SWEPT_FACE",FACE,{"disambiguationData":[OSD([sQuery(id+"F14.wireOp",EDGE,"E24")])]}),makeQuery(id+"F15.opExtrude","SWEPT_FACE",FACE,{"disambiguationData":[OSD([sQuery(id+"F14.wireOp",EDGE,"E28")])]})]}),makeQuery(id+"F17.opExtrude","SWEPT_FACE",FACE,{"disambiguationData":[OSD([sQuery(id+"F16.wireOp",EDGE,"E32")])]})]}),makeQuery(id+"F19.opExtrude","SWEPT_FACE",FACE,{"disambiguationData":[OSD([sQuery(id+"F18.wireOp",EDGE,"E36")])]})]}),makeQuery(id+"F25.opExtrude","SWEPT_FACE",FACE,{"disambiguationData":[OSD([sQuery(id+"F24.wireOp",EDGE,"E48")])]})]});}
            var sketch = newSketch(context, id + "F36", { "sketchPlane" : qUnion([Q0])});
            skLineSegment(sketch, "E81", {"start": v(-647.84, -102.8) * mm, "end": v(-558.4, -102.8) * mm});
            skLineSegment(sketch, "E82", {"start": v(-558.4, -102.8) * mm, "end": v(-558.4, 163.72) * mm});
            skLineSegment(sketch, "E83", {"start": v(-558.4, 163.72) * mm, "end": v(-647.84, 163.72) * mm});
            skLineSegment(sketch, "E84", {"start": v(-647.84, 163.72) * mm, "end": v(-647.84, -102.8) * mm});
            skSolve(sketch);
        }
        {
            var Q0;
            Q0 = qSketchRegion(id + "F36", true);
            extrude(context, id + "F37", {"entities" : qUnion([Q0]), "operationType" : NewBodyOperationType.ADD, "depth" : 38.1 * mm, "offsetDistance" : 25.4 * mm});
        }
        {
            var Q0;
            {var subQ1=sQuery(id+"F3.wireOp",EDGE,"E1");var subQ2=makeQuery(id+"F5.opShell","OFFSET_FACE",FACE,{"disambiguationData":[OSD([subQ1])]});var subQ3=sQuery(id+"F3.wireOp",EDGE,"E4");var subQ6=sQuery(id+"F0.wireOp",EDGE,"E0.bottom");var subQ8=makeQuery(id+"F7.opExtrude","SWEPT_FACE",FACE,{"disambiguationData":[OSD([sQuery(id+"F6.wireOp",EDGE,"E7")])]});var subQ9=sQuery(id+"F0.wireOp",EDGE,"E0.right");var subQ11=sQuery(id+"F0.wireOp",EDGE,"E0.left");var subQ12=sQuery(id+"F0.wireOp",EDGE,"E0.top");var subQ13=makeQuery(id+"F5.opShell","OFFSET_FACE",FACE,{"disambiguationData":[OSD([subQ6,subQ12,subQ11,subQ9,subQ3])]});var subQ14=makeQuery(id+"F9.boolean.opBoolean","MERGE",FACE,{"derivedFrom":[makeQuery(id+"F7.boolean.opBoolean","SPLIT",FACE,{"disambiguationData":[TD([subQ2])],"derivedFrom":subQ13}),makeQuery(id+"F7.boolean.opBoolean","SPLIT",FACE,{"disambiguationData":[TD([subQ8])],"derivedFrom":subQ13}),makeQuery(id+"F9.opExtrude","SWEPT_FACE",FACE,{"disambiguationData":[OSD([sQuery(id+"F8.wireOp",EDGE,"E12")])]})]});Q0=makeQuery(id+"F25.boolean.opBoolean","MERGE",FACE,{"derivedFrom":[makeQuery(id+"F19.boolean.opBoolean","MERGE",FACE,{"derivedFrom":[makeQuery(id+"F17.boolean.opBoolean","MERGE",FACE,{"derivedFrom":[makeQuery(id+"F15.boolean.opBoolean","MERGE",FACE,{"derivedFrom":[makeQuery(id+"F11.boolean.opBoolean","SPLIT",FACE,{"disambiguationData":[TD([makeQuery(id+"F11.opExtrude","SWEPT_FACE",FACE,{"disambiguationData":[OSD([sQuery(id+"F10.wireOp",EDGE,"E15")])]})])],"derivedFrom":subQ14}),makeQuery(id+"F13.boolean.opBoolean","MERGE",FACE,{"derivedFrom":[makeQuery(id+"F2.opShell","OFFSET_FACE",FACE,{"disambiguationData":[OSD([subQ6,subQ12,subQ11,subQ9])]}),makeQuery(id+"F11.boolean.opBoolean","SPLIT",FACE,{"disambiguationData":[TD([subQ2])],"derivedFrom":subQ14}),makeQuery(id+"F13.opExtrude","SWEPT_FACE",FACE,{"disambiguationData":[OSD([sQuery(id+"F12.wireOp",EDGE,"E20")])]})]}),makeQuery(id+"F15.opExtrude","SWEPT_FACE",FACE,{"disambiguationData":[OSD([sQuery(id+"F14.wireOp",EDGE,"E24")])]}),makeQuery(id+"F15.opExtrude","SWEPT_FACE",FACE,{"disambiguationData":[OSD([sQuery(id+"F14.wireOp",EDGE,"E28")])]})]}),makeQuery(id+"F17.opExtrude","SWEPT_FACE",FACE,{"disambiguationData":[OSD([sQuery(id+"F16.wireOp",EDGE,"E32")])]})]}),makeQuery(id+"F19.opExtrude","SWEPT_FACE",FACE,{"disambiguationData":[OSD([sQuery(id+"F18.wireOp",EDGE,"E36")])]})]}),makeQuery(id+"F25.opExtrude","SWEPT_FACE",FACE,{"disambiguationData":[OSD([sQuery(id+"F24.wireOp",EDGE,"E48")])]})]});}
            var sketch = newSketch(context, id + "F38", { "sketchPlane" : qUnion([Q0])});
            skCircle(sketch, "E85", {"center": v(-397.51, 0) * mm, "radius": 105.78 * mm});
            skSolve(sketch);
        }
        {
            var Q0;
            Q0 = qSketchRegion(id + "F38", true);
            extrude(context, id + "F39", {"entities" : qUnion([Q0]), "operationType" : NewBodyOperationType.ADD, "depth" : 38.1 * mm, "offsetDistance" : 25.4 * mm});
        }
        {
            var Q0;
            {var subQ1=sQuery(id+"F3.wireOp",EDGE,"E1");var subQ2=makeQuery(id+"F5.opShell","OFFSET_FACE",FACE,{"disambiguationData":[OSD([subQ1])]});var subQ3=sQuery(id+"F3.wireOp",EDGE,"E4");var subQ6=sQuery(id+"F0.wireOp",EDGE,"E0.bottom");var subQ8=makeQuery(id+"F7.opExtrude","SWEPT_FACE",FACE,{"disambiguationData":[OSD([sQuery(id+"F6.wireOp",EDGE,"E7")])]});var subQ9=sQuery(id+"F0.wireOp",EDGE,"E0.right");var subQ11=sQuery(id+"F0.wireOp",EDGE,"E0.left");var subQ12=sQuery(id+"F0.wireOp",EDGE,"E0.top");var subQ13=makeQuery(id+"F5.opShell","OFFSET_FACE",FACE,{"disambiguationData":[OSD([subQ6,subQ12,subQ11,subQ9,subQ3])]});var subQ14=makeQuery(id+"F9.boolean.opBoolean","MERGE",FACE,{"derivedFrom":[makeQuery(id+"F7.boolean.opBoolean","SPLIT",FACE,{"disambiguationData":[TD([subQ2])],"derivedFrom":subQ13}),makeQuery(id+"F7.boolean.opBoolean","SPLIT",FACE,{"disambiguationData":[TD([subQ8])],"derivedFrom":subQ13}),makeQuery(id+"F9.opExtrude","SWEPT_FACE",FACE,{"disambiguationData":[OSD([sQuery(id+"F8.wireOp",EDGE,"E12")])]})]});Q0=makeQuery(id+"F25.boolean.opBoolean","MERGE",FACE,{"derivedFrom":[makeQuery(id+"F19.boolean.opBoolean","MERGE",FACE,{"derivedFrom":[makeQuery(id+"F17.boolean.opBoolean","MERGE",FACE,{"derivedFrom":[makeQuery(id+"F15.boolean.opBoolean","MERGE",FACE,{"derivedFrom":[makeQuery(id+"F11.boolean.opBoolean","SPLIT",FACE,{"disambiguationData":[TD([makeQuery(id+"F11.opExtrude","SWEPT_FACE",FACE,{"disambiguationData":[OSD([sQuery(id+"F10.wireOp",EDGE,"E15")])]})])],"derivedFrom":subQ14}),makeQuery(id+"F13.boolean.opBoolean","MERGE",FACE,{"derivedFrom":[makeQuery(id+"F2.opShell","OFFSET_FACE",FACE,{"disambiguationData":[OSD([subQ6,subQ12,subQ11,subQ9])]}),makeQuery(id+"F11.boolean.opBoolean","SPLIT",FACE,{"disambiguationData":[TD([subQ2])],"derivedFrom":subQ14}),makeQuery(id+"F13.opExtrude","SWEPT_FACE",FACE,{"disambiguationData":[OSD([sQuery(id+"F12.wireOp",EDGE,"E20")])]})]}),makeQuery(id+"F15.opExtrude","SWEPT_FACE",FACE,{"disambiguationData":[OSD([sQuery(id+"F14.wireOp",EDGE,"E24")])]}),makeQuery(id+"F15.opExtrude","SWEPT_FACE",FACE,{"disambiguationData":[OSD([sQuery(id+"F14.wireOp",EDGE,"E28")])]})]}),makeQuery(id+"F17.opExtrude","SWEPT_FACE",FACE,{"disambiguationData":[OSD([sQuery(id+"F16.wireOp",EDGE,"E32")])]})]}),makeQuery(id+"F19.opExtrude","SWEPT_FACE",FACE,{"disambiguationData":[OSD([sQuery(id+"F18.wireOp",EDGE,"E36")])]})]}),makeQuery(id+"F25.opExtrude","SWEPT_FACE",FACE,{"disambiguationData":[OSD([sQuery(id+"F24.wireOp",EDGE,"E48")])]})]});}
            var sketch = newSketch(context, id + "F40", { "sketchPlane" : qUnion([Q0])});
            skCircle(sketch, "E86", {"center": v(36.96, -29.67) * mm, "radius": 157.67 * mm});
            skSolve(sketch);
        }
        {
            var Q0;
            Q0 = qSketchRegion(id + "F40", true);
            extrude(context, id + "F41", {"entities" : qUnion([Q0]), "operationType" : NewBodyOperationType.ADD, "depth" : 38.1 * mm, "offsetDistance" : 25.4 * mm});
        }
    });
